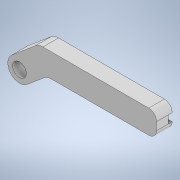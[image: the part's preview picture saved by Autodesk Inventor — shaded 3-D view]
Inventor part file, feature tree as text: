
AUTODESK INVENTOR PART (.ipt)
format: ipt  version: 2020 (Build 240168000, 168)  size: 127,488 bytes
history: native  units: mm
features: extrude x2, sketch x2
ambient origin geometry x8: Origin, YZ Plane, XZ Plane, XY Plane, X Axis, Y Axis, Z Axis, Center Point
bodies: Solid1 (feature_tree)
feature tree (4):
  extrude  "Extrusion1"  Depth=6.0mm
  extrude  "Extrusion3"  Depth=1.0mm
  sketch  "Sketch1"  dims[d0=6.0mm d1=6.0mm]
  sketch  "Sketch3"  dims[d2=3.0mm d3=24.43461mm d4=2.0mm d5=2.0mm d6=35.0mm d7=3.5mm d8=4.0mm d9=0.0mm d14=28.0mm d15=2.0mm d16=1.0mm d17=0.0mm]
